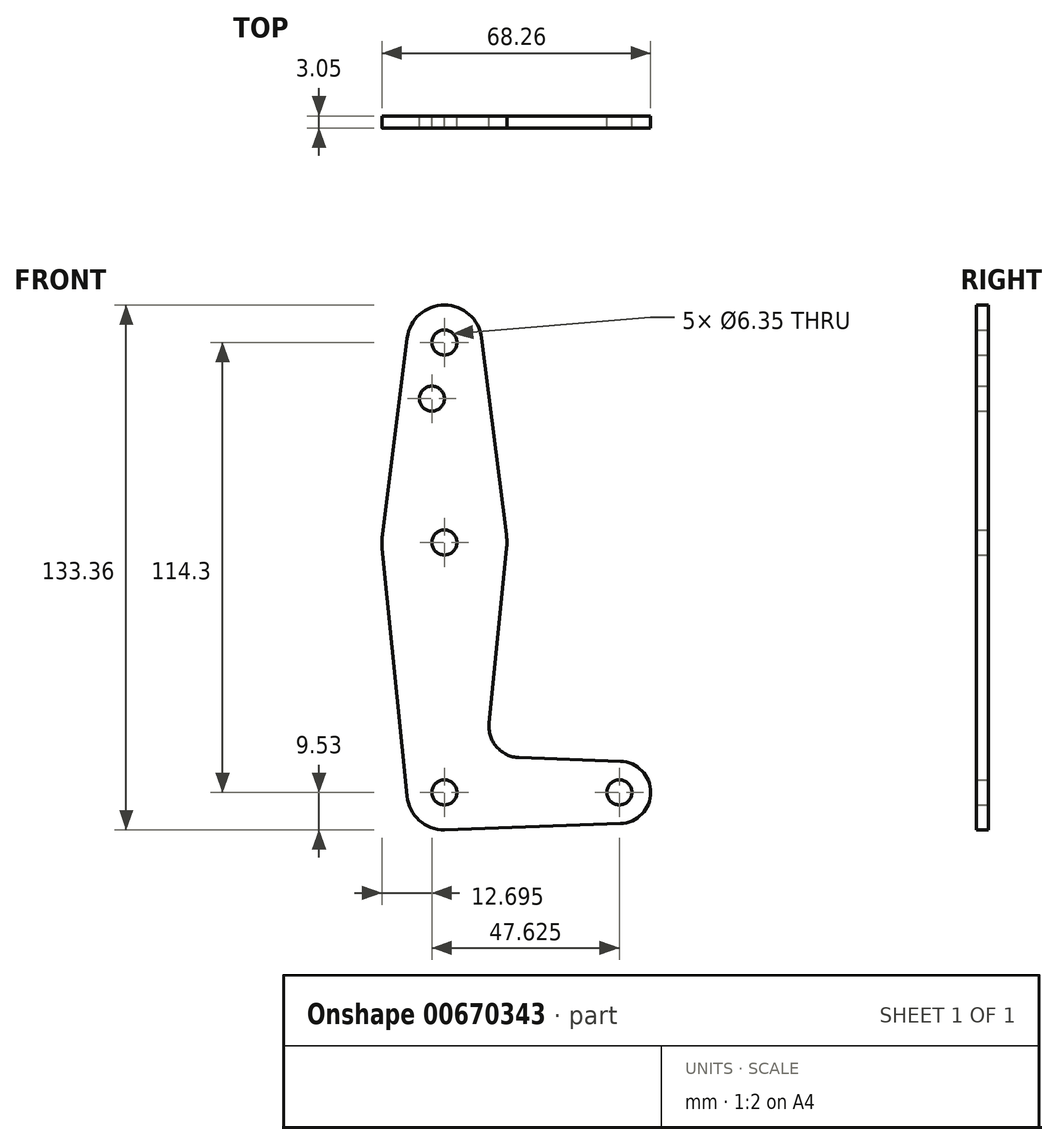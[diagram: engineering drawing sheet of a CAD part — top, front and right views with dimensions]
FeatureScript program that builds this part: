
annotation { "Feature Type Name" : "Feature", "Feature Type Description" : "" }
export const myFeature = defineFeature(function(context is Context, id is Id, definition is map)
    precondition{}
    {
        {
            var Q0;
            Q0=qCreatedBy(makeId("Front.planeOp"),FACE);
            var sketch = newSketch(context, id + "F0", { "sketchPlane" : qUnion([Q0])});
            skLineSegment(sketch, "E0", {"start": v(0, 0) * mm, "end": v(0, 114.3) * mm, "construction": true});
            skLineSegment(sketch, "E1", {"start": v(0, 0) * mm, "end": v(44.45, 0) * mm, "construction": true});
            skCircle(sketch, "E2", {"center": v(0, 0) * mm, "radius": 9.53 * mm});
            skCircle(sketch, "E3", {"center": v(0, 114.3) * mm, "radius": 9.53 * mm});
            skCircle(sketch, "E4", {"center": v(0, 63.5) * mm, "radius": 15.88 * mm});
            skCircle(sketch, "E5", {"center": v(44.45, 0) * mm, "radius": 7.94 * mm});
            skLineSegment(sketch, "E6", {"start": v(-9.45, 115.5) * mm, "end": v(-15.75, 65.48) * mm});
            skLineSegment(sketch, "E7", {"start": v(9.45, 115.5) * mm, "end": v(15.75, 65.48) * mm});
            skCircle(sketch, "E8", {"center": v(0, 114.3) * mm, "radius": 3.18 * mm});
            skCircle(sketch, "E9", {"center": v(0, 63.5) * mm, "radius": 3.18 * mm});
            skCircle(sketch, "E10", {"center": v(0, 0) * mm, "radius": 3.18 * mm});
            skCircle(sketch, "E11", {"center": v(44.45, 0) * mm, "radius": 3.18 * mm});
            skCircle(sketch, "E12", {"center": v(-3.18, 100.03) * mm, "radius": 3.18 * mm});
            skLineSegment(sketch, "E13", {"start": v(18.97, 8.85) * mm, "end": v(44.73, 7.93) * mm});
            skLineSegment(sketch, "E14", {"start": v(15.8, 61.91) * mm, "end": v(11.34, 17.59) * mm});
            skLineSegment(sketch, "E15", {"start": v(-15.8, 61.91) * mm, "end": v(-9.48, -0.95) * mm});
            skLineSegment(sketch, "E16", {"start": v(0, -9.53) * mm, "end": v(44.73, -7.93) * mm});
            skPoint(sketch, "E17.newPointA", {"position": v(0, 9.53) * mm});
            skArc(sketch, "E17.filletArc", {"start": v(11.34, 17.59) * mm, "mid": v(13.26, 11.57) * mm, "end": v(18.97, 8.85) * mm});
            skSolve(sketch);
        }
        {
            var Q0;
            {var subQ0=sQuery(id+"F0.wireOp",EDGE,"E13");Q0=makeQuery(id+"F0.imprint","IMPRINT",FACE,{"disambiguationData":[TD([[makeQuery(id+"F0.imprint","IMPRINT",EDGE,{"derivedFrom":subQ0}),-1.0]])]});}
            var Q1;
            {var subQ1=sQuery(id+"F0.wireOp",EDGE,"E6");Q1=makeQuery(id+"F0.imprint","IMPRINT",FACE,{"disambiguationData":[TD([[makeQuery(id+"F0.imprint","IMPRINT",EDGE,{"derivedFrom":subQ1}),1.0]])]});}
            var Q2;
            Q2=makeQuery(id+"F0.imprint","IMPRINT",FACE,{"disambiguationData":[TD([[makeQuery(id+"F0.imprint","IMPRINT",EDGE,{"derivedFrom":sQuery(id+"F0.wireOp",EDGE,"E8")}),-1.0]])]});
            var Q3;
            Q3=makeQuery(id+"F0.imprint","IMPRINT",FACE,{"disambiguationData":[TD([[makeQuery(id+"F0.imprint","IMPRINT",EDGE,{"derivedFrom":sQuery(id+"F0.wireOp",EDGE,"E9")}),-1.0]])]});
            var Q4;
            Q4=makeQuery(id+"F0.imprint","IMPRINT",FACE,{"disambiguationData":[TD([[makeQuery(id+"F0.imprint","IMPRINT",EDGE,{"derivedFrom":sQuery(id+"F0.wireOp",EDGE,"E10")}),-1.0]])]});
            var Q5;
            Q5=makeQuery(id+"F0.imprint","IMPRINT",FACE,{"disambiguationData":[TD([[makeQuery(id+"F0.imprint","IMPRINT",EDGE,{"derivedFrom":sQuery(id+"F0.wireOp",EDGE,"E11")}),-1.0]])]});
            extrude(context, id + "F1", {"entities" : qUnion([Q0, Q1, Q2, Q3, Q4, Q5]), "depth" : 3.05 * mm, "offsetDistance" : 25.4 * mm});
        }
    });
